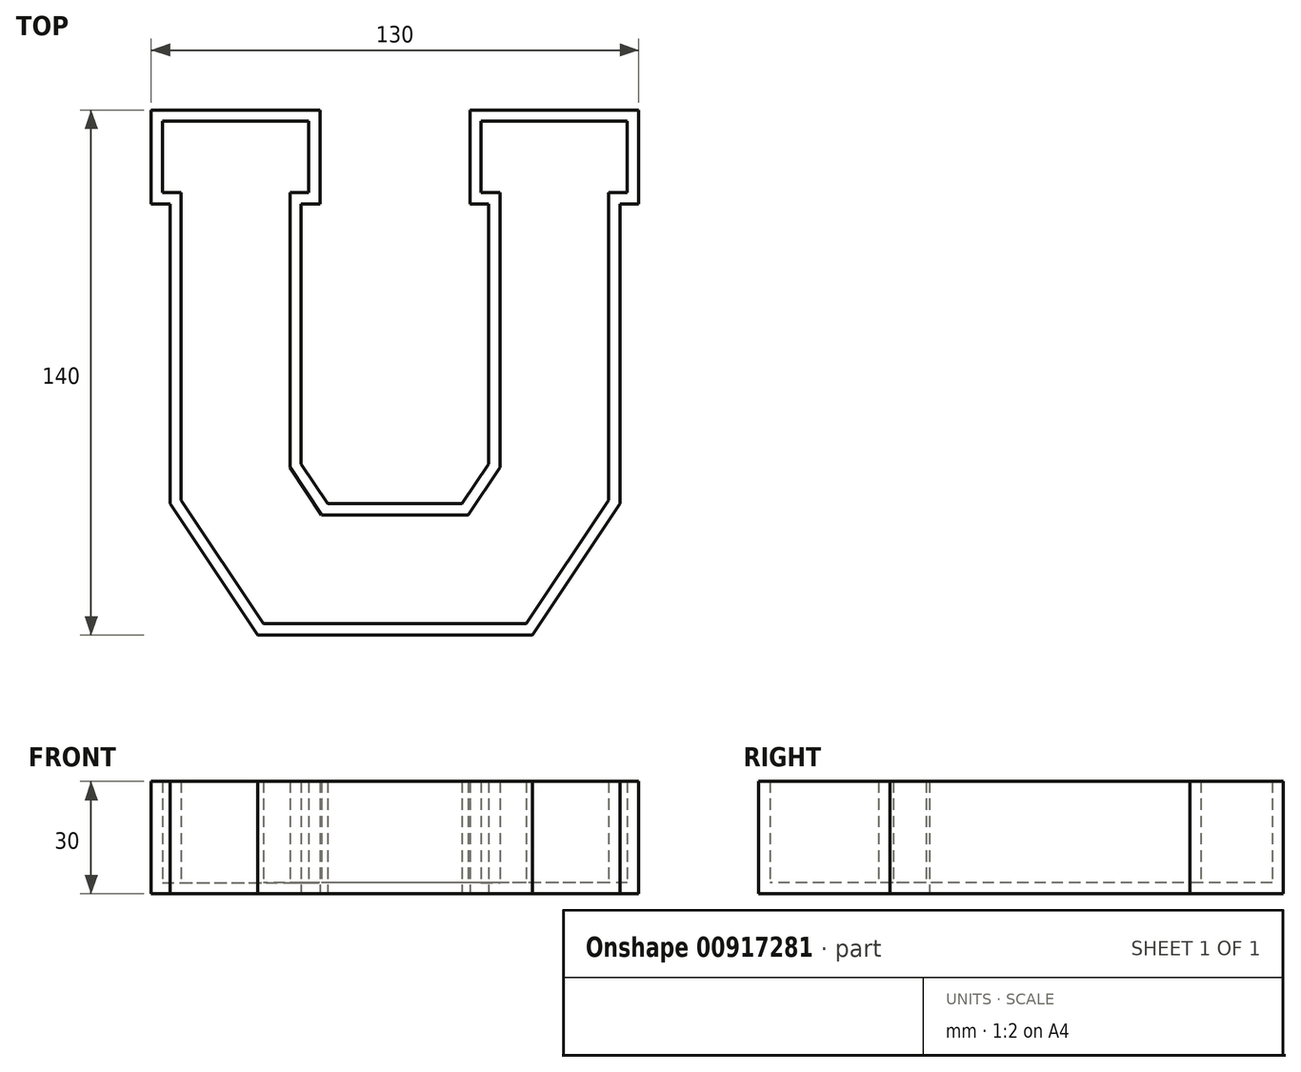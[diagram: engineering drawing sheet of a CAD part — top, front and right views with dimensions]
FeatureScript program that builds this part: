
annotation { "Feature Type Name" : "Feature", "Feature Type Description" : "" }
export const myFeature = defineFeature(function(context is Context, id is Id, definition is map)
    precondition{}
    {
        {
            var Q0;
            Q0=qCreatedBy(makeId("Top.planeOp"),FACE);
            var sketch = newSketch(context, id + "F0", { "sketchPlane" : qUnion([Q0])});
            skLineSegment(sketch, "E0", {"start": v(-65, 70) * mm, "end": v(-65, 45) * mm});
            skLineSegment(sketch, "E1", {"start": v(-65, 45) * mm, "end": v(-60, 45) * mm});
            skLineSegment(sketch, "E2", {"start": v(-60, 45) * mm, "end": v(-60, -35) * mm});
            skLineSegment(sketch, "E3", {"start": v(-60, -35) * mm, "end": v(-36.67, -70) * mm});
            skLineSegment(sketch, "E4", {"start": v(-36.67, -70) * mm, "end": v(0, -70) * mm});
            skLineSegment(sketch, "E5", {"start": v(-65, 70) * mm, "end": v(-20, 70) * mm});
            skLineSegment(sketch, "E6", {"start": v(-20, 70) * mm, "end": v(-20, 45) * mm});
            skLineSegment(sketch, "E7", {"start": v(-20, 45) * mm, "end": v(-25, 45) * mm});
            skLineSegment(sketch, "E8", {"start": v(-25, 45) * mm, "end": v(-25, -24.4) * mm});
            skLineSegment(sketch, "E9", {"start": v(-25, -24.4) * mm, "end": v(-17.94, -35) * mm});
            skLineSegment(sketch, "E10", {"start": v(-17.94, -35) * mm, "end": v(0, -35) * mm});
            skLineSegment(sketch, "E11.MirrorCS", {"start": v(65, 45) * mm, "end": v(60, 45) * mm});
            skLineSegment(sketch, "E12.MirrorCS", {"start": v(20, 45) * mm, "end": v(25, 45) * mm});
            skLineSegment(sketch, "E13.MirrorCS", {"start": v(25, -24.4) * mm, "end": v(17.94, -35) * mm});
            skLineSegment(sketch, "E14.MirrorCS", {"start": v(60, -35) * mm, "end": v(36.67, -70) * mm});
            skLineSegment(sketch, "E15.MirrorCS", {"start": v(25, 45) * mm, "end": v(25, -24.4) * mm});
            skLineSegment(sketch, "E16.MirrorCS", {"start": v(36.67, -70) * mm, "end": v(0, -70) * mm});
            skLineSegment(sketch, "E17.MirrorCS", {"start": v(20, 70) * mm, "end": v(20, 45) * mm});
            skLineSegment(sketch, "E18.MirrorCS", {"start": v(65, 70) * mm, "end": v(65, 45) * mm});
            skLineSegment(sketch, "E19.MirrorCS", {"start": v(65, 70) * mm, "end": v(20, 70) * mm});
            skLineSegment(sketch, "E20.MirrorCS", {"start": v(60, 45) * mm, "end": v(60, -35) * mm});
            skLineSegment(sketch, "E21.MirrorCS", {"start": v(17.94, -35) * mm, "end": v(0, -35) * mm});
            skSolve(sketch);
        }
        {
            var Q0;
            Q0 = qSketchRegion(id + "F0", true);
            extrude(context, id + "F1", {"entities" : qUnion([Q0]), "depth" : 30 * mm, "offsetDistance" : 25 * mm});
        }
        {
            var Q0;
            Q0=makeQuery(id+"F1.opExtrude","CAP_FACE",FACE,{"disambiguationData":[OSD([sQuery(id+"F0.wireOp",EDGE,"E0"),sQuery(id+"F0.wireOp",EDGE,"E1"),sQuery(id+"F0.wireOp",EDGE,"E2"),sQuery(id+"F0.wireOp",EDGE,"E3"),sQuery(id+"F0.wireOp",EDGE,"E4"),sQuery(id+"F0.wireOp",EDGE,"E5"),sQuery(id+"F0.wireOp",EDGE,"E6"),sQuery(id+"F0.wireOp",EDGE,"E7"),sQuery(id+"F0.wireOp",EDGE,"E8"),sQuery(id+"F0.wireOp",EDGE,"E9"),sQuery(id+"F0.wireOp",EDGE,"E10"),sQuery(id+"F0.wireOp",EDGE,"E11.MirrorCS"),sQuery(id+"F0.wireOp",EDGE,"E12.MirrorCS"),sQuery(id+"F0.wireOp",EDGE,"E13.MirrorCS"),sQuery(id+"F0.wireOp",EDGE,"E14.MirrorCS"),sQuery(id+"F0.wireOp",EDGE,"E15.MirrorCS"),sQuery(id+"F0.wireOp",EDGE,"E16.MirrorCS"),sQuery(id+"F0.wireOp",EDGE,"E17.MirrorCS"),sQuery(id+"F0.wireOp",EDGE,"E18.MirrorCS"),sQuery(id+"F0.wireOp",EDGE,"E19.MirrorCS"),sQuery(id+"F0.wireOp",EDGE,"E20.MirrorCS"),sQuery(id+"F0.wireOp",EDGE,"E21.MirrorCS")])],"isStart":false});
            shell(context, id + "F2", {"entities" : qUnion([Q0]), "thickness" : 3 * mm});
        }
    });
